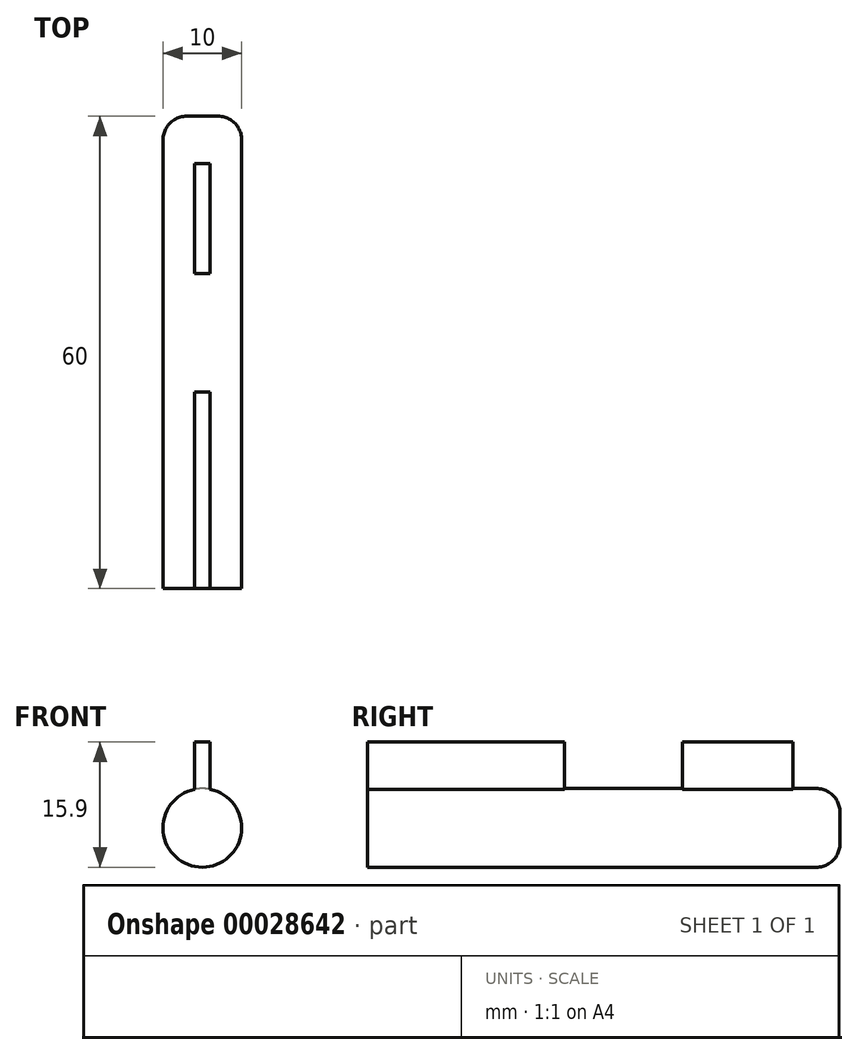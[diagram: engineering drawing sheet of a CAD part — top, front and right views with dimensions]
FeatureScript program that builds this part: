
annotation { "Feature Type Name" : "Feature", "Feature Type Description" : "" }
export const myFeature = defineFeature(function(context is Context, id is Id, definition is map)
    precondition{}
    {
        {
            var Q0;
            Q0=qCreatedBy(makeId("Right.planeOp"),FACE);
            var sketch = newSketch(context, id + "F0", { "sketchPlane" : qUnion([Q0])});
            skLineSegment(sketch, "E0", {"start": v(-93.78, 0) * mm, "end": v(31.88, 0) * mm, "construction": true});
            skLineSegment(sketch, "E1", {"start": v(-45, 0) * mm, "end": v(-45, 2.5) * mm});
            skLineSegment(sketch, "E2", {"start": v(-45, 2.5) * mm, "end": v(-20, 2.5) * mm});
            skLineSegment(sketch, "E3", {"start": v(-20, 2.5) * mm, "end": v(-20, 5) * mm});
            skLineSegment(sketch, "E4", {"start": v(-20, 5) * mm, "end": v(0, 5) * mm});
            skLineSegment(sketch, "E5", {"start": v(0, 5) * mm, "end": v(0, 0) * mm});
            skLineSegment(sketch, "E6", {"start": v(-45, 0) * mm, "end": v(0, 0) * mm});
            skSolve(sketch);
        }
        {
            var Q0;
            Q0=makeQuery(id+"F0.imprint","IMPRINT",FACE,{"disambiguationData":[TD([[makeQuery(id+"F0.imprint","IMPRINT",EDGE,{"derivedFrom":sQuery(id+"F0.wireOp",EDGE,"E1")}),-1.0]])]});
            var Q1;
            Q1=sQuery(id+"F0.wireOp",EDGE,"E0");
            revolve(context, id + "F1", {"entities" : qUnion([Q0]), "axis" : qUnion([Q1]), "revolveType" : RevolveType.FULL});
        }
        {
            var Q0;
            Q0=makeQuery(id+"F1.opRevolve","SWEPT_EDGE",EDGE,{"disambiguationData":[OSD([sQuery(id+"F0.wireOp",EDGE,"E4"),sQuery(id+"F0.wireOp",EDGE,"E5")])]});
            fillet(context, id + "F2", {"entities" : qUnion([Q0]), "radius" : 3 * mm, "tangentPropagation" : true, "allowEdgeOverflow" : false});
        }
        {
            var Q0;
            Q0=makeQuery(id+"F1.opRevolve","SWEPT_EDGE",EDGE,{"disambiguationData":[OSD([sQuery(id+"F0.wireOp",EDGE,"E1"),sQuery(id+"F0.wireOp",EDGE,"E2")])]});
            chamfer(context, id + "F3", {"entities" : qUnion([Q0]), "width" : 2 * mm, "tangentPropagation" : true});
        }
        {
            var Q0;
            Q0=makeQuery(id+"F1.opRevolve","SWEPT_FACE",FACE,{"disambiguationData":[OSD([sQuery(id+"F0.wireOp",EDGE,"E3")])]});
            var sketch = newSketch(context, id + "F4", { "sketchPlane" : qUnion([Q0])});
            skCircle(sketch, "E7", {"center": v(0, 0) * mm, "radius": 5 * mm});
            skLineSegment(sketch, "E8.bottom", {"start": v(-1, 4.9) * mm, "end": v(1, 4.9) * mm});
            skLineSegment(sketch, "E8.top", {"start": v(-1, 10.9) * mm, "end": v(1, 10.9) * mm});
            skLineSegment(sketch, "E8.left", {"start": v(-1, 4.9) * mm, "end": v(-1, 10.9) * mm});
            skLineSegment(sketch, "E8.right", {"start": v(1, 4.9) * mm, "end": v(1, 10.9) * mm});
            skSolve(sketch);
        }
        {
            var Q0;
            Q0=makeQuery(id+"F4.imprint","IMPRINT",FACE,{"disambiguationData":[TD([[makeQuery(id+"F4.imprint","IMPRINT",EDGE,{"derivedFrom":makeQuery(id+"F1.opRevolve","SWEPT_EDGE",EDGE,{"disambiguationData":[OSD([sQuery(id+"F0.wireOp",EDGE,"E2"),sQuery(id+"F0.wireOp",EDGE,"E3")])]})}),1.0]])]});
            var Q1;
            {var subQ0=sQuery(id+"F4.wireOp",EDGE,"E8.bottom");Q1=makeQuery(id+"F4.imprint","IMPRINT",FACE,{"disambiguationData":[TD([[makeQuery(id+"F4.imprint","IMPRINT",EDGE,{"derivedFrom":subQ0}),1.0]])]});}
            var Q2;
            {var subQ0=sQuery(id+"F4.wireOp",EDGE,"E8.bottom");Q2=makeQuery(id+"F4.imprint","IMPRINT",FACE,{"disambiguationData":[TD([[makeQuery(id+"F4.imprint","IMPRINT",EDGE,{"derivedFrom":subQ0}),-1.0]])]});}
            extrude(context, id + "F5", {"entities" : qUnion([Q0, Q1, Q2]), "depth" : 40 * mm});
        }
        {
            var Q0;
            Q0=makeQuery(id+"F1.opRevolve","SWEPT_BODY",BODY,{"disambiguationData":[OSD([sQuery(id+"F0.wireOp",EDGE,"E1"),sQuery(id+"F0.wireOp",EDGE,"E2"),sQuery(id+"F0.wireOp",EDGE,"E3"),sQuery(id+"F0.wireOp",EDGE,"E4"),sQuery(id+"F0.wireOp",EDGE,"E5"),sQuery(id+"F0.wireOp",EDGE,"E6")])]});
            var Q1;
            Q1=makeQuery(id+"F5.opExtrude","SWEPT_BODY",BODY,{"disambiguationData":[OSD([sQuery(id+"F4.wireOp",EDGE,"E7")])]});
            var Q2;
            Q2=makeQuery(id+"F3.opChamfer","BLEND_FACE",FACE,{"disambiguationData":[OSD([sQuery(id+"F0.wireOp",EDGE,"E1"),sQuery(id+"F0.wireOp",EDGE,"E2")])]});
            var Q3;
            Q3=makeQuery(id+"F1.opRevolve","SWEPT_FACE",FACE,{"disambiguationData":[OSD([sQuery(id+"F0.wireOp",EDGE,"E1")])]});
            booleanBodies(context, id + "F6", {"operationType" : BooleanOperationType.SUBTRACTION, "tools" : qUnion([Q0]), "targets" : qUnion([Q1]), "entitiesToOffset" : qUnion([Q2, Q3]), "oppositeDirection" : true, "keepTools" : true});
        }
        {
            var Q0;
            Q0=makeQuery(id+"F4.imprint","IMPRINT",FACE,{"disambiguationData":[TD([[makeQuery(id+"F4.imprint","IMPRINT",EDGE,{"derivedFrom":sQuery(id+"F4.wireOp",EDGE,"E8.top")}),-1.0]])]});
            var Q1;
            Q1=makeQuery(id+"F2.opFillet","BLEND_FACE",FACE,{"disambiguationData":[OSD([sQuery(id+"F0.wireOp",EDGE,"E4"),sQuery(id+"F0.wireOp",EDGE,"E5")])]});
            extrude(context, id + "F7", {"entities" : qUnion([Q0]), "operationType" : NewBodyOperationType.ADD, "oppositeDirection" : true, "endBoundEntityFace" : qUnion([Q1]), "depth" : 14 * mm});
        }
        {
            var Q0;
            Q0=makeQuery(id+"F4.imprint","IMPRINT",FACE,{"disambiguationData":[TD([[makeQuery(id+"F4.imprint","IMPRINT",EDGE,{"derivedFrom":sQuery(id+"F4.wireOp",EDGE,"E8.top")}),-1.0]])]});
            cPlane(context, id + "F8", {"entities" : qUnion([Q0]), "cplaneType" : CPlaneType.OFFSET, "offset" : 15 * mm, "width" : 150 * mm, "height" : 150 * mm});
        }
        {
            var Q0;
            Q0=qCreatedBy(id+"F8.planeOp",FACE);
            var sketch = newSketch(context, id + "F9", { "sketchPlane" : qUnion([Q0])});
            skLineSegment(sketch, "E9.0.0", {"start": v(1, 10.9) * mm, "end": v(-1, 10.9) * mm});
            skLineSegment(sketch, "E9.0.1", {"start": v(-1, 10.9) * mm, "end": v(-1, 4.9) * mm});
            skArc(sketch, "E9.0.2", {"start": v(-1, 4.9) * mm, "mid": v(0, 5) * mm, "end": v(1, 4.9) * mm});
            skLineSegment(sketch, "E9.0.3", {"start": v(1, 4.9) * mm, "end": v(1, 10.9) * mm});
            skSolve(sketch);
        }
        {
            var Q0;
            Q0 = qSketchRegion(id + "F9", true);
            var Q1;
            Q1=makeQuery(id+"F5.opExtrude","CAP_FACE",FACE,{"disambiguationData":[OSD([sQuery(id+"F4.wireOp",EDGE,"E7")])],"isStart":false});
            extrude(context, id + "F10", {"entities" : qUnion([Q0]), "operationType" : NewBodyOperationType.ADD, "endBound" : BoundingType.UP_TO_SURFACE, "endBoundEntityFace" : qUnion([Q1]), "depth" : 25 * mm});
        }
    });
